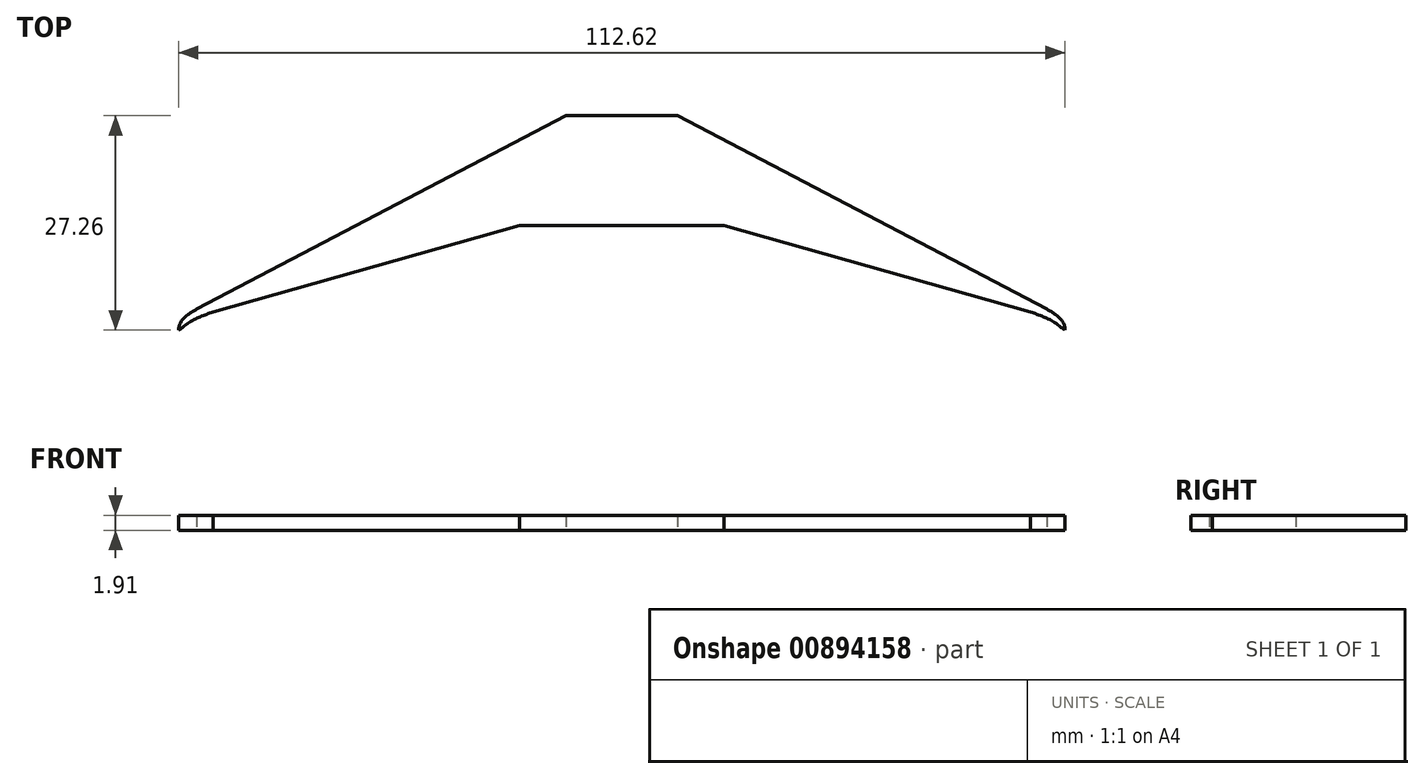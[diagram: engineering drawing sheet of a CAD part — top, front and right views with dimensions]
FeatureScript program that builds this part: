
annotation { "Feature Type Name" : "Feature", "Feature Type Description" : "" }
export const myFeature = defineFeature(function(context is Context, id is Id, definition is map)
    precondition{}
    {
        {
            var Q0;
            Q0=qCreatedBy(makeId("Top.planeOp"),FACE);
            var sketch = newSketch(context, id + "F0", { "sketchPlane" : qUnion([Q0])});
            skLineSegment(sketch, "E0", {"start": v(0, 13.32) * mm, "end": v(12.98, 13.32) * mm});
            skLineSegment(sketch, "E1", {"start": v(12.98, 13.32) * mm, "end": v(51.93, 2.32) * mm});
            skFitSpline(sketch, "E2", {"points": [v(51.93, 2.32) * mm, v(52.89, 1.97) * mm, v(53.84, 1.58) * mm, v(54.83, 1.08) * mm, v(55.89, 0.3) * mm, v(56.31, 0) * mm], "startDerivative": vector(4.72, -1.65) * mm, "endDerivative": vector(2.58, -1.7) * mm});
            skFitSpline(sketch, "E3", {"points": [v(56.31, 0) * mm, v(56.1, 0.9) * mm, v(55.1, 1.97) * mm, v(53.99, 2.68) * mm], "startDerivative": vector(-0.29, 3.07) * mm, "endDerivative": vector(-3.23, 1.79) * mm});
            skLineSegment(sketch, "E4.MirrorCS", {"start": v(-12.98, 13.32) * mm, "end": v(-51.93, 2.32) * mm});
            skLineSegment(sketch, "E5.MirrorCS", {"start": v(0, 13.32) * mm, "end": v(-12.98, 13.32) * mm});
            skFitSpline(sketch, "E6.MirrorCS", {"points": [v(-51.93, 2.32) * mm, v(-52.89, 1.97) * mm, v(-53.84, 1.58) * mm, v(-54.83, 1.08) * mm, v(-55.89, 0.3) * mm, v(-56.31, 0) * mm], "startDerivative": vector(-4.72, -1.65) * mm, "endDerivative": vector(-2.58, -1.7) * mm});
            skFitSpline(sketch, "E7.MirrorCS", {"points": [v(-56.31, 0) * mm, v(-56.1, 0.9) * mm, v(-55.1, 1.97) * mm, v(-53.99, 2.68) * mm], "startDerivative": vector(0.29, 3.07) * mm, "endDerivative": vector(3.23, 1.79) * mm});
            skLineSegment(sketch, "E8", {"start": v(0, 27.26) * mm, "end": v(7.1, 27.26) * mm});
            skLineSegment(sketch, "E9", {"start": v(7.1, 27.26) * mm, "end": v(53.99, 2.68) * mm});
            skLineSegment(sketch, "E10.MirrorCS", {"start": v(0, 27.26) * mm, "end": v(-7.1, 27.26) * mm});
            skLineSegment(sketch, "E11.MirrorCS", {"start": v(-7.1, 27.26) * mm, "end": v(-53.99, 2.68) * mm});
            skLineSegment(sketch, "E12", {"start": v(14.56, 21.65) * mm, "end": v(5.87, 26.2) * mm});
            skLineSegment(sketch, "E13", {"start": v(50.85, 3.5) * mm, "end": v(18.37, 20.53) * mm});
            skLineSegment(sketch, "E14", {"start": v(50.85, 3.5) * mm, "end": v(51.43, 4.02) * mm});
            skLineSegment(sketch, "E15", {"start": v(18.37, 20.53) * mm, "end": v(19, 21.03) * mm});
            skLineSegment(sketch, "E16", {"start": v(14.56, 21.65) * mm, "end": v(15.82, 22.7) * mm});
            skLineSegment(sketch, "E17", {"start": v(5.87, 26.2) * mm, "end": v(7.1, 27.26) * mm});
            skLineSegment(sketch, "E18.MirrorCS", {"start": v(-5.87, 26.2) * mm, "end": v(-7.1, 27.26) * mm});
            skLineSegment(sketch, "E19.MirrorCS", {"start": v(-14.56, 21.65) * mm, "end": v(-5.87, 26.2) * mm});
            skLineSegment(sketch, "E20.MirrorCS", {"start": v(-14.56, 21.65) * mm, "end": v(-15.82, 22.7) * mm});
            skLineSegment(sketch, "E21.MirrorCS", {"start": v(-18.37, 20.53) * mm, "end": v(-19, 21.03) * mm});
            skLineSegment(sketch, "E22.MirrorCS", {"start": v(-50.85, 3.5) * mm, "end": v(-18.37, 20.53) * mm});
            skLineSegment(sketch, "E23.MirrorCS", {"start": v(-50.85, 3.5) * mm, "end": v(-51.43, 4.02) * mm});
            skLineSegment(sketch, "E24", {"start": v(0, 27.26) * mm, "end": v(0, 13.32) * mm});
            skLineSegment(sketch, "E25", {"start": v(0, 16.1) * mm, "end": v(13.04, 16.1) * mm});
            skLineSegment(sketch, "E26", {"start": v(13.04, 16.1) * mm, "end": v(12.98, 13.32) * mm});
            skLineSegment(sketch, "E27", {"start": v(13.04, 16.1) * mm, "end": v(41.73, 6.53) * mm});
            skLineSegment(sketch, "E28", {"start": v(41.73, 6.53) * mm, "end": v(46.17, 5.27) * mm});
            skLineSegment(sketch, "E29", {"start": v(46.17, 5.27) * mm, "end": v(45.56, 4.12) * mm});
            skLineSegment(sketch, "E30", {"start": v(41.73, 6.53) * mm, "end": v(41.33, 5.31) * mm});
            skLineSegment(sketch, "E31", {"start": v(41.15, 6.72) * mm, "end": v(40.8, 5.46) * mm});
            skLineSegment(sketch, "E32", {"start": v(15.26, 15.36) * mm, "end": v(14.44, 12.9) * mm});
            skLineSegment(sketch, "E33", {"start": v(0, 16.61) * mm, "end": v(13.15, 16.61) * mm});
            skLineSegment(sketch, "E34", {"start": v(1.78, 19.63) * mm, "end": v(1.78, 16.61) * mm});
            skLineSegment(sketch, "E35", {"start": v(13.15, 16.61) * mm, "end": v(41.31, 7.21) * mm});
            skLineSegment(sketch, "E36", {"start": v(41.31, 7.21) * mm, "end": v(41.15, 6.72) * mm});
            skLineSegment(sketch, "E37", {"start": v(1.78, 19.63) * mm, "end": v(1.47, 19.63) * mm});
            skLineSegment(sketch, "E38", {"start": v(1.47, 19.63) * mm, "end": v(1.47, 16.61) * mm});
            skLineSegment(sketch, "E39", {"start": v(2.9, 16.61) * mm, "end": v(2.9, 19.61) * mm});
            skLineSegment(sketch, "E40", {"start": v(2.9, 19.61) * mm, "end": v(3.27, 19.61) * mm});
            skLineSegment(sketch, "E41", {"start": v(3.27, 19.61) * mm, "end": v(3.27, 16.61) * mm});
            skLineSegment(sketch, "E42.MirrorCS", {"start": v(0, 16.1) * mm, "end": v(-13.04, 16.1) * mm});
            skLineSegment(sketch, "E43.MirrorCS", {"start": v(0, 16.61) * mm, "end": v(-13.15, 16.61) * mm});
            skLineSegment(sketch, "E44.MirrorCS", {"start": v(-13.04, 16.1) * mm, "end": v(-12.98, 13.32) * mm});
            skLineSegment(sketch, "E45.MirrorCS", {"start": v(-15.26, 15.36) * mm, "end": v(-14.44, 12.9) * mm});
            skLineSegment(sketch, "E46.MirrorCS", {"start": v(-13.04, 16.1) * mm, "end": v(-41.73, 6.53) * mm});
            skLineSegment(sketch, "E47.MirrorCS", {"start": v(-13.15, 16.61) * mm, "end": v(-41.31, 7.21) * mm});
            skLineSegment(sketch, "E48.MirrorCS", {"start": v(-1.47, 19.63) * mm, "end": v(-1.47, 16.61) * mm});
            skLineSegment(sketch, "E49.MirrorCS", {"start": v(-1.78, 19.63) * mm, "end": v(-1.78, 16.61) * mm});
            skLineSegment(sketch, "E50.MirrorCS", {"start": v(-2.9, 16.61) * mm, "end": v(-2.9, 19.61) * mm});
            skLineSegment(sketch, "E51.MirrorCS", {"start": v(-3.27, 19.61) * mm, "end": v(-3.27, 16.61) * mm});
            skLineSegment(sketch, "E52.MirrorCS", {"start": v(-2.9, 19.61) * mm, "end": v(-3.27, 19.61) * mm});
            skLineSegment(sketch, "E53.MirrorCS", {"start": v(-1.78, 19.63) * mm, "end": v(-1.47, 19.63) * mm});
            skLineSegment(sketch, "E54.MirrorCS", {"start": v(-41.31, 7.21) * mm, "end": v(-41.15, 6.72) * mm});
            skLineSegment(sketch, "E55.MirrorCS", {"start": v(-41.15, 6.72) * mm, "end": v(-40.8, 5.46) * mm});
            skLineSegment(sketch, "E56.MirrorCS", {"start": v(-41.73, 6.53) * mm, "end": v(-41.33, 5.31) * mm});
            skLineSegment(sketch, "E57.MirrorCS", {"start": v(-41.73, 6.53) * mm, "end": v(-46.17, 5.27) * mm});
            skLineSegment(sketch, "E58.MirrorCS", {"start": v(-46.17, 5.27) * mm, "end": v(-45.56, 4.12) * mm});
            skSolve(sketch);
        }
        {
            var Q0;
            {var subQ0=sQuery(id+"F0.wireOp",EDGE,"E45.MirrorCS");Q0=makeQuery(id+"F0.imprint","IMPRINT",FACE,{"disambiguationData":[TD([[makeQuery(id+"F0.imprint","IMPRINT",EDGE,{"derivedFrom":subQ0}),-1.0]])]});}
            var Q1;
            {var subQ0=sQuery(id+"F0.wireOp",EDGE,"E31");Q1=makeQuery(id+"F0.imprint","IMPRINT",FACE,{"disambiguationData":[TD([[makeQuery(id+"F0.imprint","IMPRINT",EDGE,{"derivedFrom":subQ0}),-1.0]])]});}
            var Q2;
            Q2=makeQuery(id+"F0.imprint","IMPRINT",FACE,{"disambiguationData":[TD([[makeQuery(id+"F0.imprint","IMPRINT",EDGE,{"derivedFrom":sQuery(id+"F0.wireOp",EDGE,"E12")}),-1.0]])]});
            var Q3;
            {var subQ0=sQuery(id+"F0.wireOp",EDGE,"E0");Q3=makeQuery(id+"F0.imprint","IMPRINT",FACE,{"disambiguationData":[TD([[makeQuery(id+"F0.imprint","IMPRINT",EDGE,{"derivedFrom":subQ0}),1.0]])]});}
            var Q4;
            Q4=makeQuery(id+"F0.imprint","IMPRINT",FACE,{"disambiguationData":[TD([[makeQuery(id+"F0.imprint","IMPRINT",EDGE,{"derivedFrom":sQuery(id+"F0.wireOp",EDGE,"E28")}),-1.0]])]});
            var Q5;
            {var subQ15=sQuery(id+"F0.wireOp",EDGE,"E6.MirrorCS");Q5=makeQuery(id+"F0.imprint","IMPRINT",FACE,{"disambiguationData":[TD([[makeQuery(id+"F0.imprint","IMPRINT",EDGE,{"derivedFrom":subQ15}),-1.0]])]});}
            var Q6;
            {var subQ0=sQuery(id+"F0.wireOp",EDGE,"E56.MirrorCS");Q6=makeQuery(id+"F0.imprint","IMPRINT",FACE,{"disambiguationData":[TD([[makeQuery(id+"F0.imprint","IMPRINT",EDGE,{"derivedFrom":subQ0}),-1.0]])]});}
            var Q7;
            {var subQ12=sQuery(id+"F0.wireOp",EDGE,"E2");Q7=makeQuery(id+"F0.imprint","IMPRINT",FACE,{"disambiguationData":[TD([[makeQuery(id+"F0.imprint","IMPRINT",EDGE,{"derivedFrom":subQ12}),1.0]])]});}
            var Q8;
            {var subQ0=sQuery(id+"F0.wireOp",EDGE,"E18.MirrorCS");Q8=makeQuery(id+"F0.imprint","IMPRINT",FACE,{"disambiguationData":[TD([[makeQuery(id+"F0.imprint","IMPRINT",EDGE,{"derivedFrom":subQ0}),1.0]])]});}
            var Q9;
            {var subQ0=sQuery(id+"F0.wireOp",EDGE,"E5.MirrorCS");Q9=makeQuery(id+"F0.imprint","IMPRINT",FACE,{"disambiguationData":[TD([[makeQuery(id+"F0.imprint","IMPRINT",EDGE,{"derivedFrom":subQ0}),-1.0]])]});}
            var Q10;
            {var subQ0=sQuery(id+"F0.wireOp",EDGE,"E21.MirrorCS");Q10=makeQuery(id+"F0.imprint","IMPRINT",FACE,{"disambiguationData":[TD([[makeQuery(id+"F0.imprint","IMPRINT",EDGE,{"derivedFrom":subQ0}),1.0]])]});}
            var Q11;
            {var subQ1=sQuery(id+"F0.wireOp",EDGE,"E42.MirrorCS");Q11=makeQuery(id+"F0.imprint","IMPRINT",FACE,{"disambiguationData":[TD([[makeQuery(id+"F0.imprint","IMPRINT",EDGE,{"derivedFrom":subQ1}),-1.0]])]});}
            var Q12;
            Q12=makeQuery(id+"F0.imprint","IMPRINT",FACE,{"disambiguationData":[TD([[makeQuery(id+"F0.imprint","IMPRINT",EDGE,{"derivedFrom":sQuery(id+"F0.wireOp",EDGE,"E13")}),-1.0]])]});
            var Q13;
            {var subQ7=sQuery(id+"F0.wireOp",EDGE,"E25");Q13=makeQuery(id+"F0.imprint","IMPRINT",FACE,{"disambiguationData":[TD([[makeQuery(id+"F0.imprint","IMPRINT",EDGE,{"derivedFrom":subQ7}),1.0]])]});}
            var Q14;
            {var subQ0=sQuery(id+"F0.wireOp",EDGE,"E44.MirrorCS");Q14=makeQuery(id+"F0.imprint","IMPRINT",FACE,{"disambiguationData":[TD([[makeQuery(id+"F0.imprint","IMPRINT",EDGE,{"derivedFrom":subQ0}),-1.0]])]});}
            var Q15;
            {var subQ0=sQuery(id+"F0.wireOp",EDGE,"E26");Q15=makeQuery(id+"F0.imprint","IMPRINT",FACE,{"disambiguationData":[TD([[makeQuery(id+"F0.imprint","IMPRINT",EDGE,{"derivedFrom":subQ0}),1.0]])]});}
            var Q16;
            {var subQ0=sQuery(id+"F0.wireOp",EDGE,"E48.MirrorCS");Q16=makeQuery(id+"F0.imprint","IMPRINT",FACE,{"disambiguationData":[TD([[makeQuery(id+"F0.imprint","IMPRINT",EDGE,{"derivedFrom":subQ0}),-1.0]])]});}
            var Q17;
            {var subQ0=sQuery(id+"F0.wireOp",EDGE,"E34");Q17=makeQuery(id+"F0.imprint","IMPRINT",FACE,{"disambiguationData":[TD([[makeQuery(id+"F0.imprint","IMPRINT",EDGE,{"derivedFrom":subQ0}),-1.0]])]});}
            var Q18;
            {var subQ0=sQuery(id+"F0.wireOp",EDGE,"E39");Q18=makeQuery(id+"F0.imprint","IMPRINT",FACE,{"disambiguationData":[TD([[makeQuery(id+"F0.imprint","IMPRINT",EDGE,{"derivedFrom":subQ0}),-1.0]])]});}
            var Q19;
            {var subQ0=sQuery(id+"F0.wireOp",EDGE,"E50.MirrorCS");Q19=makeQuery(id+"F0.imprint","IMPRINT",FACE,{"disambiguationData":[TD([[makeQuery(id+"F0.imprint","IMPRINT",EDGE,{"derivedFrom":subQ0}),1.0]])]});}
            var Q20;
            {var subQ0=sQuery(id+"F0.wireOp",EDGE,"E30");Q20=makeQuery(id+"F0.imprint","IMPRINT",FACE,{"disambiguationData":[TD([[makeQuery(id+"F0.imprint","IMPRINT",EDGE,{"derivedFrom":subQ0}),-1.0]])]});}
            var Q21;
            {var subQ0=sQuery(id+"F0.wireOp",EDGE,"E55.MirrorCS");Q21=makeQuery(id+"F0.imprint","IMPRINT",FACE,{"disambiguationData":[TD([[makeQuery(id+"F0.imprint","IMPRINT",EDGE,{"derivedFrom":subQ0}),-1.0]])]});}
            extrude(context, id + "F1", {"entities" : qUnion([Q0, Q1, Q2, Q3, Q4, Q5, Q6, Q7, Q8, Q9, Q10, Q11, Q12, Q13, Q14, Q15, Q16, Q17, Q18, Q19, Q20, Q21]), "depth" : 1.9 * mm, "offsetDistance" : 25.4 * mm});
        }
    });
